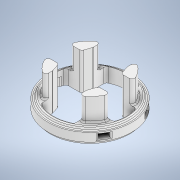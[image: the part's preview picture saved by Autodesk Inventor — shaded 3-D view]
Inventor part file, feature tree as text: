
AUTODESK INVENTOR PART (.ipt)
format: ipt  version: 2020 (Build 240168000, 168)  size: 393,728 bytes
history: native  units: in
note: dims shown in document units (in); Inventor stores cm internally (conversion verified against a paired STEP export)
features: sketch x4, extrude x3, fillet x2, mirror x2, revolve x1, hole x1
ambient origin geometry x8: Origin, YZ Plane, XZ Plane, XY Plane, X Axis, Y Axis, Z Axis, Center Point
bodies: Solid1 (feature_tree)
feature tree (13):
  revolve  "Revolution1"  [1 undecoded]
  sketch  "Sketch2"  dims[d2=1.85in d3=1.5in]
  extrude  "Extrusion1"  Depth=1.5in
  extrude  "Extrusion3"  TaperAngle=90.0deg  [1 undecoded]
  fillet  "Fillet2"  Radius=0.5in
  hole  "Hole1"  [1 undecoded]
  extrude  "Extrusion2"  Depth=0.0625in
  mirror  "Mirror1"
  mirror  "Mirror2"
  fillet  "Fillet1"  [1 undecoded]
  sketch  "Sketch1"  dims[d0=1.745in d1=0.125in]
  sketch  "Sketch3"  dims[d5=0.5in d6=90.0deg d7=0.5in]
  sketch  "Sketch4"  dims[d10=1.756in d11=0.0625in d15=1.5in d16=0.0in d17=0.0in d18=0.125in d19=3.25in d21=2.5in d22=1.5in d23=0.205in d24=0.75in d25=0.375in d26=0.25in d27=0.5635in d28=0.4375in d29=0.0in d30=0.385in d31=0.25in d32=0.0in d33=120.0deg d35=0.125in d36=1.0in d37=2.4in d38=0.375in d39=0.0in d43=0.4947in d44=0.4947in d45=0.13in d46=1.5in d40=0.5in d41=0.0344in]
note: 4 required parameter values undecoded (feature->parameter linkage not recoverable at this tier; creation-order binding heuristic only, values carry confidence <= 0.55)